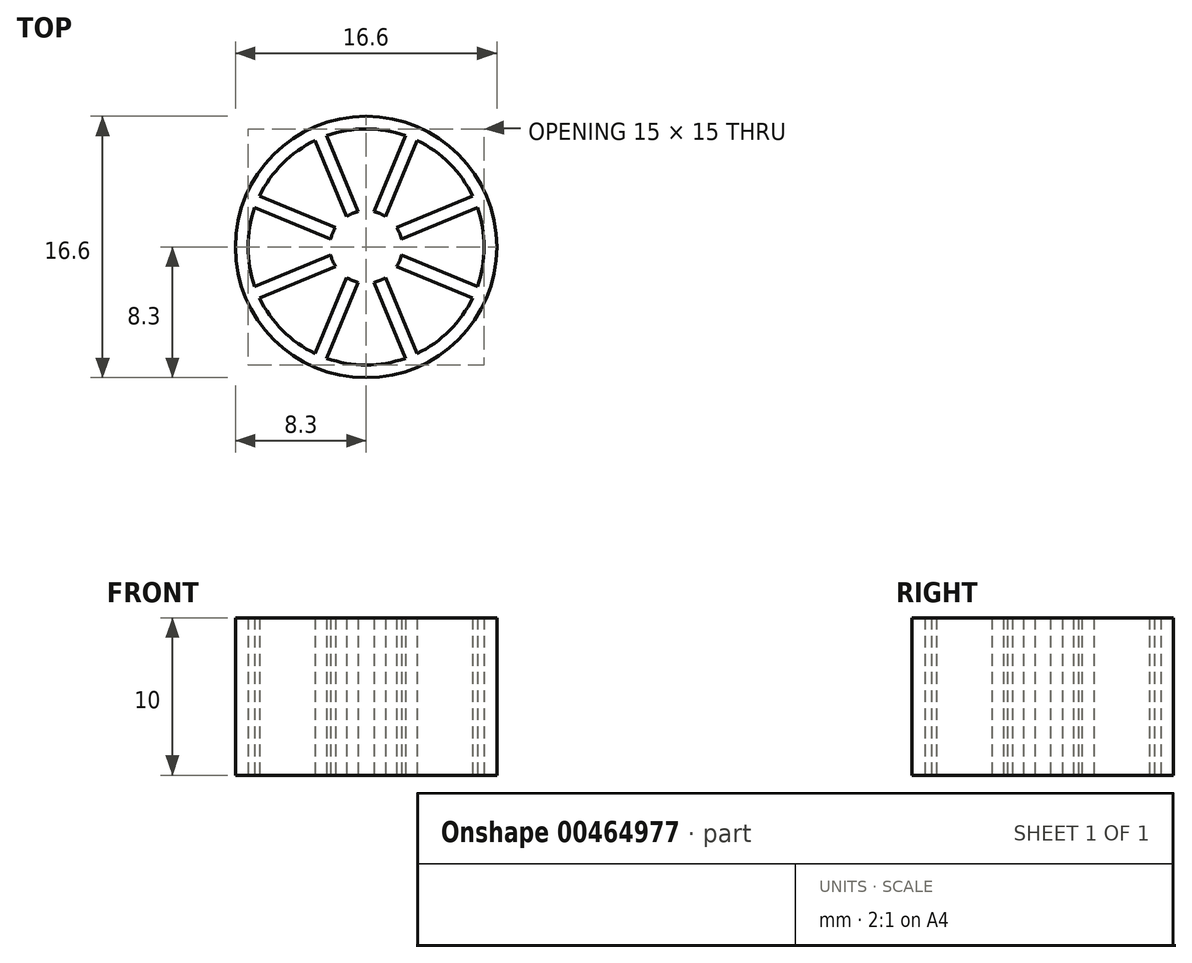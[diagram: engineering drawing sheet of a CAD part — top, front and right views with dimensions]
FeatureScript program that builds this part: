
annotation { "Feature Type Name" : "Feature", "Feature Type Description" : "" }
export const myFeature = defineFeature(function(context is Context, id is Id, definition is map)
    precondition{}
    {
        {
            var Q0;
            Q0=qCreatedBy(makeId("Top.planeOp"),FACE);
            var sketch = newSketch(context, id + "F0", { "sketchPlane" : qUnion([Q0])});
            skArc(sketch, "E0", {"start": v(0, 7.5) * mm, "mid": v(-1.27, 7.4) * mm, "end": v(-2.5, 7.07) * mm});
            skArc(sketch, "E1", {"start": v(-1.94, 1.24) * mm, "mid": v(-2.12, 0.88) * mm, "end": v(-2.25, 0.5) * mm});
            skArc(sketch, "E2", {"start": v(0, 8.3) * mm, "mid": v(-5.87, 5.87) * mm, "end": v(-8.3, 0) * mm});
            skLineSegment(sketch, "E3", {"start": v(-2.87, 6.93) * mm, "end": v(0, 0) * mm, "construction": true});
            skLineSegment(sketch, "E4", {"start": v(-3.24, 6.77) * mm, "end": v(-1.24, 1.94) * mm});
            skLineSegment(sketch, "E5", {"start": v(-0.5, 2.25) * mm, "end": v(-2.5, 7.07) * mm});
            skLineSegment(sketch, "E6", {"start": v(0, 0) * mm, "end": v(-6.93, 2.87) * mm, "construction": true});
            skLineSegment(sketch, "E7", {"start": v(-1.94, 1.24) * mm, "end": v(-6.77, 3.24) * mm});
            skLineSegment(sketch, "E8", {"start": v(-2.25, 0.5) * mm, "end": v(-7.07, 2.5) * mm});
            skLineSegment(sketch, "E9", {"start": v(0, 15.38) * mm, "end": v(0, -15.62) * mm, "construction": true});
            skLineSegment(sketch, "E10", {"start": v(-19.16, 0) * mm, "end": v(18.79, 0) * mm, "construction": true});
            skArc(sketch, "E11.trimOffspring", {"start": v(-0.5, 2.25) * mm, "mid": v(-0.88, 2.12) * mm, "end": v(-1.24, 1.94) * mm});
            skArc(sketch, "E12.trimOffspring", {"start": v(-3.24, 6.77) * mm, "mid": v(-5.3, 5.3) * mm, "end": v(-6.77, 3.24) * mm});
            skArc(sketch, "E13.trimOffspring", {"start": v(-7.07, 2.5) * mm, "mid": v(-7.4, 1.27) * mm, "end": v(-7.5, 0) * mm});
            skArc(sketch, "E14.MirrorCS", {"start": v(0, 7.5) * mm, "mid": v(1.27, 7.4) * mm, "end": v(2.5, 7.07) * mm});
            skArc(sketch, "E15.MirrorCS", {"start": v(0, 8.3) * mm, "mid": v(5.87, 5.87) * mm, "end": v(8.3, 0) * mm});
            skLineSegment(sketch, "E16.MirrorCS", {"start": v(0.5, 2.25) * mm, "end": v(2.5, 7.07) * mm});
            skArc(sketch, "E17.MirrorCS", {"start": v(0.5, 2.25) * mm, "mid": v(0.88, 2.12) * mm, "end": v(1.24, 1.94) * mm});
            skLineSegment(sketch, "E18.MirrorCS", {"start": v(3.24, 6.77) * mm, "end": v(1.24, 1.94) * mm});
            skArc(sketch, "E19.MirrorCS", {"start": v(3.24, 6.77) * mm, "mid": v(5.3, 5.3) * mm, "end": v(6.77, 3.24) * mm});
            skArc(sketch, "E20.MirrorCS", {"start": v(7.07, 2.5) * mm, "mid": v(7.4, 1.27) * mm, "end": v(7.5, 0) * mm});
            skLineSegment(sketch, "E21.MirrorCS", {"start": v(2.25, 0.5) * mm, "end": v(7.07, 2.5) * mm});
            skArc(sketch, "E22.MirrorCS", {"start": v(1.94, 1.24) * mm, "mid": v(2.12, 0.88) * mm, "end": v(2.25, 0.5) * mm});
            skLineSegment(sketch, "E23.MirrorCS", {"start": v(1.94, 1.24) * mm, "end": v(6.77, 3.24) * mm});
            skArc(sketch, "E24.MirrorCS", {"start": v(0.5, -2.25) * mm, "mid": v(0.88, -2.12) * mm, "end": v(1.24, -1.94) * mm});
            skArc(sketch, "E25.MirrorCS", {"start": v(-1.94, -1.24) * mm, "mid": v(-2.12, -0.88) * mm, "end": v(-2.25, -0.5) * mm});
            skArc(sketch, "E26.MirrorCS", {"start": v(1.94, -1.24) * mm, "mid": v(2.12, -0.88) * mm, "end": v(2.25, -0.5) * mm});
            skArc(sketch, "E27.MirrorCS", {"start": v(-0.5, -2.25) * mm, "mid": v(-0.88, -2.12) * mm, "end": v(-1.24, -1.94) * mm});
            skArc(sketch, "E28.MirrorCS", {"start": v(3.24, -6.77) * mm, "mid": v(5.3, -5.3) * mm, "end": v(6.77, -3.24) * mm});
            skArc(sketch, "E29.MirrorCS", {"start": v(-7.07, -2.5) * mm, "mid": v(-7.4, -1.27) * mm, "end": v(-7.5, 0) * mm});
            skArc(sketch, "E30.MirrorCS", {"start": v(0, -7.5) * mm, "mid": v(1.27, -7.4) * mm, "end": v(2.5, -7.07) * mm});
            skArc(sketch, "E31.MirrorCS", {"start": v(0, -8.3) * mm, "mid": v(5.87, -5.87) * mm, "end": v(8.3, 0) * mm});
            skLineSegment(sketch, "E32.MirrorCS", {"start": v(2.25, -0.5) * mm, "end": v(7.07, -2.5) * mm});
            skArc(sketch, "E33.MirrorCS", {"start": v(0, -7.5) * mm, "mid": v(-1.27, -7.4) * mm, "end": v(-2.5, -7.07) * mm});
            skArc(sketch, "E34.MirrorCS", {"start": v(0, -8.3) * mm, "mid": v(-5.87, -5.87) * mm, "end": v(-8.3, 0) * mm});
            skLineSegment(sketch, "E35.MirrorCS", {"start": v(-3.24, -6.77) * mm, "end": v(-1.24, -1.94) * mm});
            skLineSegment(sketch, "E36.MirrorCS", {"start": v(-0.5, -2.25) * mm, "end": v(-2.5, -7.07) * mm});
            skLineSegment(sketch, "E37.MirrorCS", {"start": v(3.24, -6.77) * mm, "end": v(1.24, -1.94) * mm});
            skArc(sketch, "E38.MirrorCS", {"start": v(7.07, -2.5) * mm, "mid": v(7.4, -1.27) * mm, "end": v(7.5, 0) * mm});
            skLineSegment(sketch, "E39.MirrorCS", {"start": v(1.94, -1.24) * mm, "end": v(6.77, -3.24) * mm});
            skLineSegment(sketch, "E40.MirrorCS", {"start": v(0.5, -2.25) * mm, "end": v(2.5, -7.07) * mm});
            skLineSegment(sketch, "E41.MirrorCS", {"start": v(-1.94, -1.24) * mm, "end": v(-6.77, -3.24) * mm});
            skLineSegment(sketch, "E42.MirrorCS", {"start": v(-2.25, -0.5) * mm, "end": v(-7.07, -2.5) * mm});
            skArc(sketch, "E43.MirrorCS", {"start": v(-3.24, -6.77) * mm, "mid": v(-5.3, -5.3) * mm, "end": v(-6.77, -3.24) * mm});
            skSolve(sketch);
        }
        {
            var Q0;
            Q0=makeQuery(id+"F0.imprint","IMPRINT",FACE,{"disambiguationData":[TD([[makeQuery(id+"F0.imprint","IMPRINT",EDGE,{"derivedFrom":sQuery(id+"F0.wireOp",EDGE,"E0")}),-1.0]])]});
            extrude(context, id + "F1", {"entities" : qUnion([Q0]), "depth" : 10 * mm});
        }
    });
